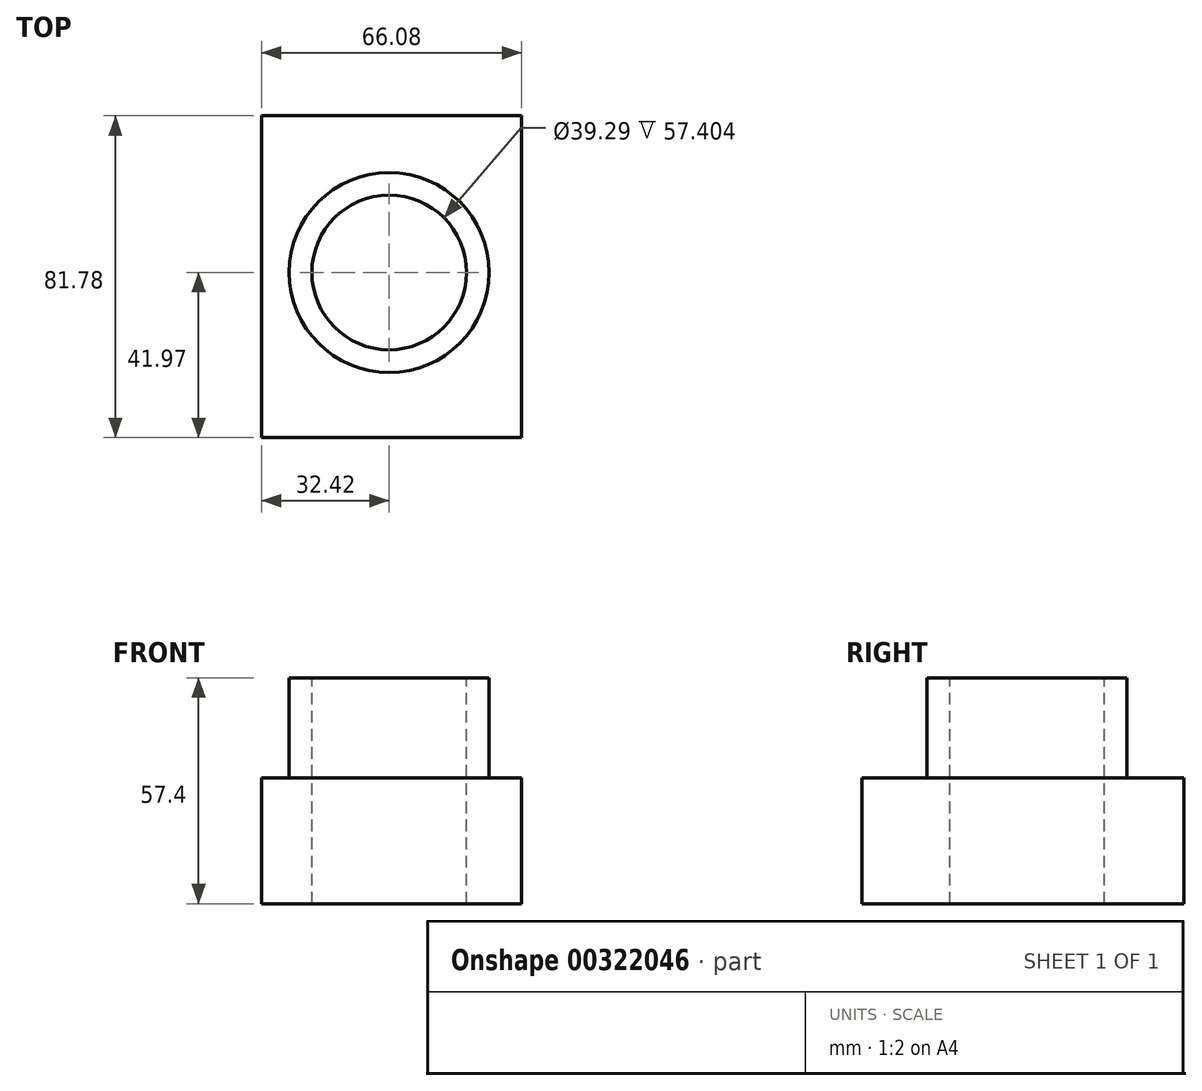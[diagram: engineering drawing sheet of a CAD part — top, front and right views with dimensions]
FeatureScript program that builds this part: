
annotation { "Feature Type Name" : "Feature", "Feature Type Description" : "" }
export const myFeature = defineFeature(function(context is Context, id is Id, definition is map)
    precondition{}
    {
        {
            var Q0;
            Q0=qCreatedBy(makeId("Top.planeOp"),FACE);
            var sketch = newSketch(context, id + "F0", { "sketchPlane" : qUnion([Q0])});
            skLineSegment(sketch, "E0.bottom", {"start": v(-32.42, 39.8) * mm, "end": v(33.66, 39.8) * mm});
            skLineSegment(sketch, "E0.top", {"start": v(-32.42, -41.97) * mm, "end": v(33.66, -41.97) * mm});
            skLineSegment(sketch, "E0.left", {"start": v(-32.42, 39.8) * mm, "end": v(-32.42, -41.97) * mm});
            skLineSegment(sketch, "E0.right", {"start": v(33.66, 39.8) * mm, "end": v(33.66, -41.97) * mm});
            skSolve(sketch);
        }
        {
            var Q0;
            Q0=makeQuery(id+"F0.imprint","IMPRINT",FACE,{"disambiguationData":[TD([[makeQuery(id+"F0.imprint","IMPRINT",EDGE,{"derivedFrom":sQuery(id+"F0.wireOp",EDGE,"E0.bottom")}),-1.0]])]});
            extrude(context, id + "F1", {"entities" : qUnion([Q0]), "depth" : 32 * mm});
        }
        {
            var Q0;
            Q0=makeQuery(id+"F1.opExtrude","CAP_FACE",FACE,{"disambiguationData":[OSD([sQuery(id+"F0.wireOp",EDGE,"E0.bottom"),sQuery(id+"F0.wireOp",EDGE,"E0.top"),sQuery(id+"F0.wireOp",EDGE,"E0.left"),sQuery(id+"F0.wireOp",EDGE,"E0.right")])],"isStart":false});
            var sketch = newSketch(context, id + "F2", { "sketchPlane" : qUnion([Q0])});
            skCircle(sketch, "E1", {"center": v(0, 0) * mm, "radius": 19.64 * mm});
            skCircle(sketch, "E2", {"center": v(0, 0) * mm, "radius": 24.44 * mm});
            skSolve(sketch);
        }
        {
            var Q0;
            Q0=makeQuery(id+"F2.imprint","IMPRINT",FACE,{"disambiguationData":[TD([[makeQuery(id+"F2.imprint","IMPRINT",EDGE,{"derivedFrom":sQuery(id+"F2.wireOp",EDGE,"E1")}),1.0]])]});
            extrude(context, id + "F3", {"entities" : qUnion([Q0]), "operationType" : NewBodyOperationType.REMOVE, "oppositeDirection" : true, "depth" : 63.25 * mm});
        }
        {
            var Q0;
            Q0=makeQuery(id+"F1.opExtrude","CAP_FACE",FACE,{"disambiguationData":[OSD([sQuery(id+"F0.wireOp",EDGE,"E0.bottom"),sQuery(id+"F0.wireOp",EDGE,"E0.top"),sQuery(id+"F0.wireOp",EDGE,"E0.left"),sQuery(id+"F0.wireOp",EDGE,"E0.right")])],"isStart":false});
            var sketch = newSketch(context, id + "F4", { "sketchPlane" : qUnion([Q0])});
            skCircle(sketch, "E3", {"center": v(0, 0) * mm, "radius": 25.4 * mm});
            skSolve(sketch);
        }
        {
            var Q0;
            Q0=makeQuery(id+"F4.imprint","IMPRINT",FACE,{"disambiguationData":[TD([[makeQuery(id+"F4.imprint","IMPRINT",EDGE,{"derivedFrom":sQuery(id+"F4.wireOp",EDGE,"E3")}),1.0]])]});
            extrude(context, id + "F5", {"entities" : qUnion([Q0]), "operationType" : NewBodyOperationType.ADD, "depth" : 25.4 * mm});
        }
    });
